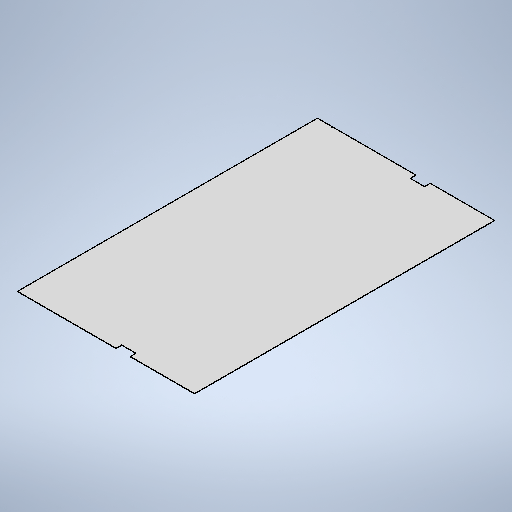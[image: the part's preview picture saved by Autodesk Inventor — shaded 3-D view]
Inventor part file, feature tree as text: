
AUTODESK INVENTOR PART (.ipt)
format: ipt  version: 2025.3 (Build 293356000, 356)  size: 303,616 bytes
history: native  units: mm
features: other x3, sketch x2, sheet_metal_op x1, projected_geometry x1
ambient origin geometry x8: Origin, YZ Plane, XZ Plane, XY Plane, X Axis, Y Axis, Z Axis, Center Point
bodies: Solid1 (feature_tree)
feature tree (7):
  sheet_metal_op  "Face1"
  sketch  "Sketch1"  dims[d2=3.0mm]
  other  "Plate1"
  sketch  "Sketch6"  dims[d22=1240.0mm d23=2100.0mm d24=40.0mm d25=40.0mm d28=100.0mm d29=410.0mm d38=2.0mm d39=5.0mm d40=0.5mm d41=3.0mm d42=2.0mm d43=5.0mm d44=3.0mm d45=5.0mm d46=100.0mm d47=3.0mm d48=0.0mm]
  projected_geometry  "Projected Loop3"
  other  "Cut1"
  other  "Definition1"
